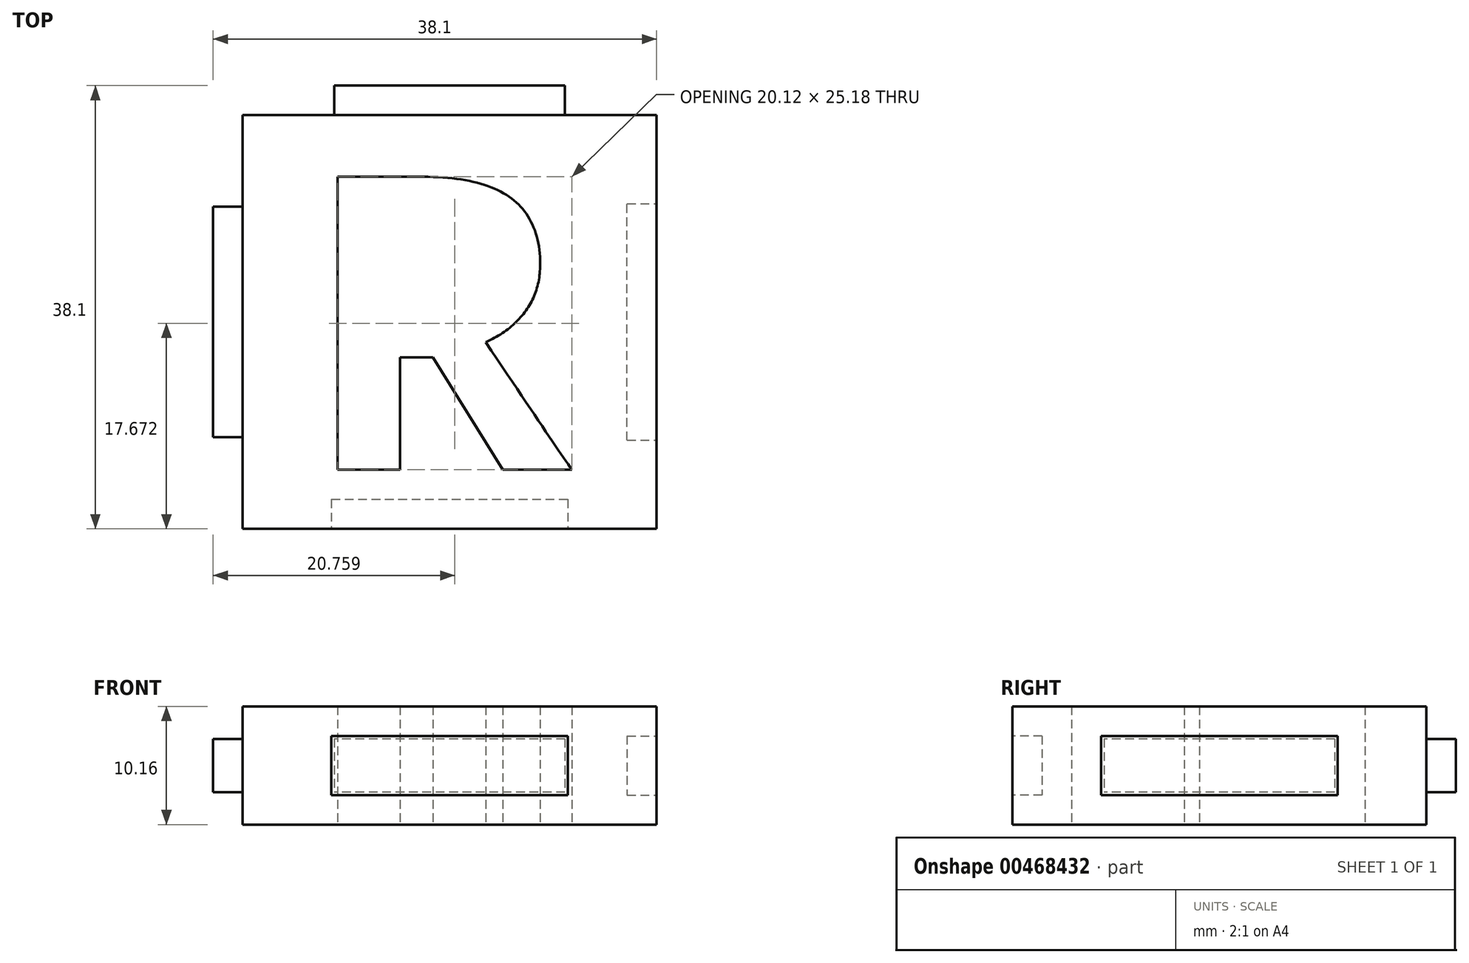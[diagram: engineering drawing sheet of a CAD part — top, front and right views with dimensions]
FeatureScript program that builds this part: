
annotation { "Feature Type Name" : "Feature", "Feature Type Description" : "" }
export const myFeature = defineFeature(function(context is Context, id is Id, definition is map)
    precondition{}
    {
        {
            var Q0;
            Q0=qCreatedBy(makeId("Top.planeOp"),FACE);
            var sketch = newSketch(context, id + "F0", { "sketchPlane" : qUnion([Q0])});
            skLineSegment(sketch, "E0.bottom", {"start": v(-17.78, 17.78) * mm, "end": v(17.78, 17.78) * mm});
            skLineSegment(sketch, "E0.top", {"start": v(-17.78, -17.78) * mm, "end": v(17.78, -17.78) * mm});
            skLineSegment(sketch, "E0.left", {"start": v(-17.78, 17.78) * mm, "end": v(-17.78, -17.78) * mm});
            skLineSegment(sketch, "E0.right", {"start": v(17.78, 17.78) * mm, "end": v(17.78, -17.78) * mm});
            skText(sketch, "E1", { "text": "R", "fontName": "OpenSans-Bold.ttf"});
            const initialGuessF0  = {"E1": [-0.01279, -0.0127, 1, 0, 0.0254]};
            skSetInitialGuess(sketch, initialGuessF0);
            skSolve(sketch);
        }
        {
            var Q0;
            Q0=qSketchRegion(id+"F0",true);
            extrude(context, id + "F1", {"entities" : qUnion([Q0]), "endBound" : BoundingType.SYMMETRIC, "depth" : 10.16 * mm});
        }
        {
            var Q0;
            Q0=makeQuery(id+"F1.opExtrude","SWEPT_FACE",FACE,{"disambiguationData":[OSD([sQuery(id+"F0.wireOp",EDGE,"E0.bottom")])]});
            var sketch = newSketch(context, id + "F2", { "sketchPlane" : qUnion([Q0])});
            skLineSegment(sketch, "E2.bottom", {"start": v(-9.9, 2.29) * mm, "end": v(9.9, 2.29) * mm});
            skLineSegment(sketch, "E2.top", {"start": v(-9.9, -2.29) * mm, "end": v(9.9, -2.29) * mm});
            skLineSegment(sketch, "E2.left", {"start": v(-9.9, 2.29) * mm, "end": v(-9.9, -2.29) * mm});
            skLineSegment(sketch, "E2.right", {"start": v(9.9, 2.29) * mm, "end": v(9.9, -2.29) * mm});
            skSolve(sketch);
        }
        {
            var Q0;
            Q0=qSketchRegion(id+"F2",true);
            extrude(context, id + "F3", {"entities" : qUnion([Q0]), "operationType" : NewBodyOperationType.ADD, "depth" : 2.54 * mm});
        }
        {
            var Q0;
            Q0=makeQuery(id+"F1.opExtrude","SWEPT_FACE",FACE,{"disambiguationData":[OSD([sQuery(id+"F0.wireOp",EDGE,"E0.left")])]});
            var sketch = newSketch(context, id + "F4", { "sketchPlane" : qUnion([Q0])});
            skLineSegment(sketch, "E3.bottom", {"start": v(-9.9, 2.29) * mm, "end": v(9.9, 2.29) * mm});
            skLineSegment(sketch, "E3.top", {"start": v(-9.9, -2.29) * mm, "end": v(9.9, -2.29) * mm});
            skLineSegment(sketch, "E3.left", {"start": v(-9.9, 2.29) * mm, "end": v(-9.9, -2.29) * mm});
            skLineSegment(sketch, "E3.right", {"start": v(9.9, 2.29) * mm, "end": v(9.9, -2.29) * mm});
            skSolve(sketch);
        }
        {
            var Q0;
            Q0=qSketchRegion(id+"F4",true);
            extrude(context, id + "F5", {"entities" : qUnion([Q0]), "operationType" : NewBodyOperationType.ADD, "depth" : 2.54 * mm});
        }
        {
            var Q0;
            Q0=makeQuery(id+"F1.opExtrude","SWEPT_FACE",FACE,{"disambiguationData":[OSD([sQuery(id+"F0.wireOp",EDGE,"E0.top")])]});
            var sketch = newSketch(context, id + "F6", { "sketchPlane" : qUnion([Q0])});
            skLineSegment(sketch, "E4.bottom", {"start": v(-10.16, 2.54) * mm, "end": v(10.16, 2.54) * mm});
            skLineSegment(sketch, "E4.top", {"start": v(-10.16, -2.54) * mm, "end": v(10.16, -2.54) * mm});
            skLineSegment(sketch, "E4.left", {"start": v(-10.16, 2.54) * mm, "end": v(-10.16, -2.54) * mm});
            skLineSegment(sketch, "E4.right", {"start": v(10.16, 2.54) * mm, "end": v(10.16, -2.54) * mm});
            skSolve(sketch);
        }
        {
            var Q0;
            Q0=qSketchRegion(id+"F6",true);
            extrude(context, id + "F7", {"entities" : qUnion([Q0]), "operationType" : NewBodyOperationType.REMOVE, "oppositeDirection" : true, "depth" : 2.54 * mm});
        }
        {
            var Q0;
            Q0=makeQuery(id+"F1.opExtrude","SWEPT_FACE",FACE,{"disambiguationData":[OSD([sQuery(id+"F0.wireOp",EDGE,"E0.right")])]});
            var sketch = newSketch(context, id + "F8", { "sketchPlane" : qUnion([Q0])});
            skLineSegment(sketch, "E5.bottom", {"start": v(-10.16, 2.54) * mm, "end": v(10.16, 2.54) * mm});
            skLineSegment(sketch, "E5.top", {"start": v(-10.16, -2.54) * mm, "end": v(10.16, -2.54) * mm});
            skLineSegment(sketch, "E5.left", {"start": v(-10.16, 2.54) * mm, "end": v(-10.16, -2.54) * mm});
            skLineSegment(sketch, "E5.right", {"start": v(10.16, 2.54) * mm, "end": v(10.16, -2.54) * mm});
            skSolve(sketch);
        }
        {
            var Q0;
            Q0=qSketchRegion(id+"F8",true);
            extrude(context, id + "F9", {"entities" : qUnion([Q0]), "operationType" : NewBodyOperationType.REMOVE, "oppositeDirection" : true, "depth" : 2.54 * mm});
        }
    });
